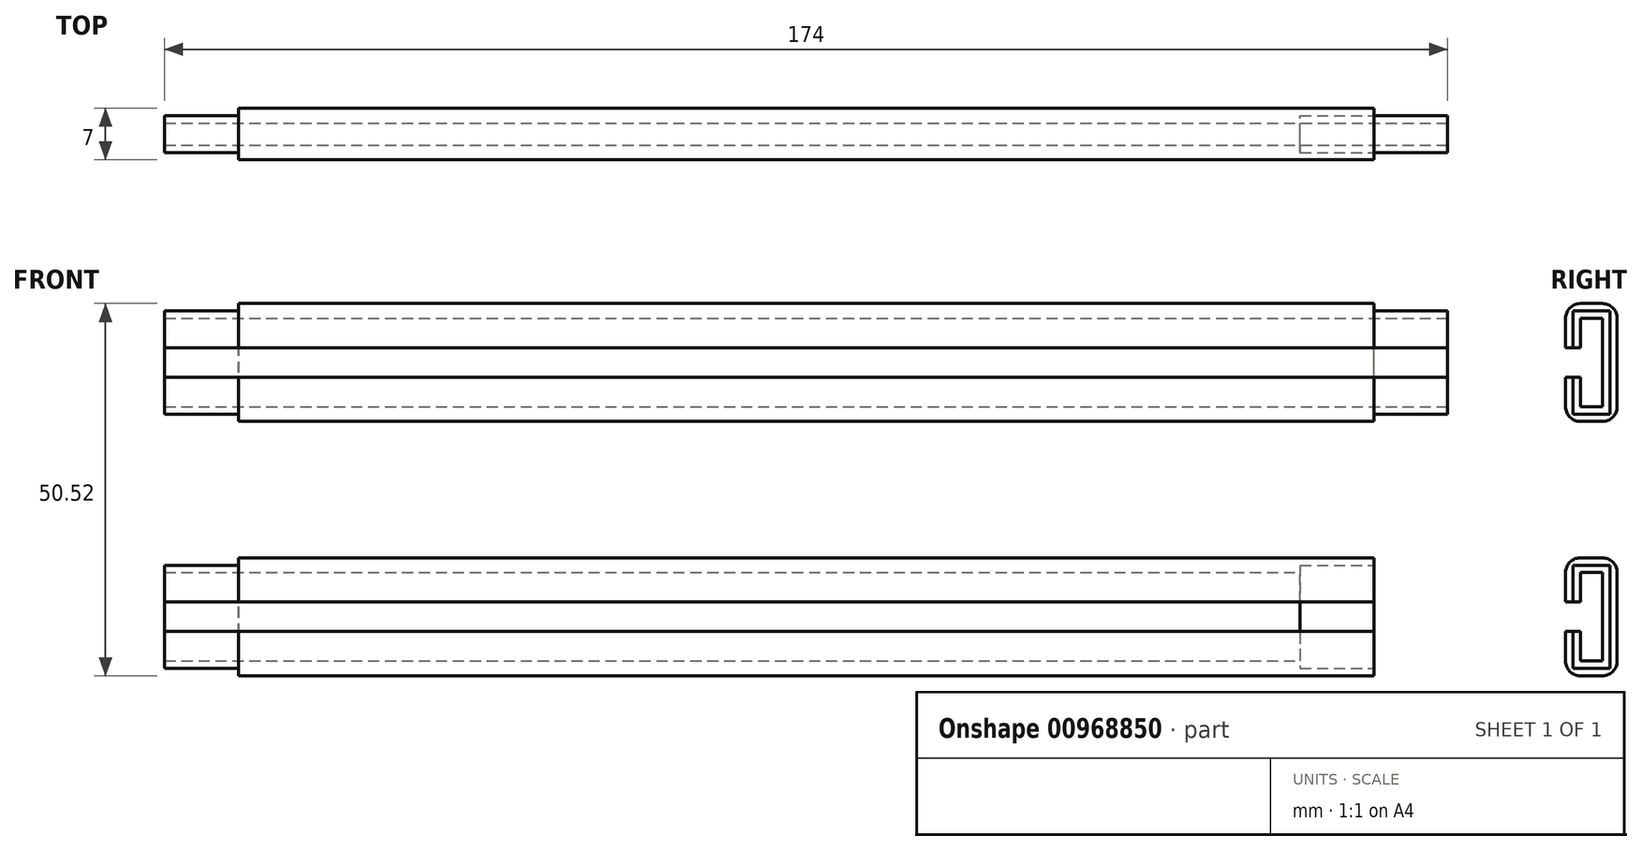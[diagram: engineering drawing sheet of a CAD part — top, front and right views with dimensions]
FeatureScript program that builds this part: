
annotation { "Feature Type Name" : "Feature", "Feature Type Description" : "" }
export const myFeature = defineFeature(function(context is Context, id is Id, definition is map)
    precondition{}
    {
        {
            var Q0;
            Q0=qCreatedBy(makeId("Front.planeOp"),FACE);
            var sketch = newSketch(context, id + "F0", { "sketchPlane" : qUnion([Q0])});
            skLineSegment(sketch, "E0.bottom", {"start": v(-19.62, 9.26) * mm, "end": v(144.38, 9.26) * mm});
            skLineSegment(sketch, "E0.top", {"start": v(-19.62, 25.26) * mm, "end": v(144.38, 25.26) * mm});
            skLineSegment(sketch, "E0.left", {"start": v(-19.62, 9.26) * mm, "end": v(-19.62, 25.26) * mm});
            skLineSegment(sketch, "E0.right", {"start": v(144.38, 9.26) * mm, "end": v(144.38, 25.26) * mm});
            skSolve(sketch);
        }
        {
            var Q0;
            Q0=makeQuery(id+"F0.imprint","IMPRINT",FACE,{"disambiguationData":[TD([[makeQuery(id+"F0.imprint","IMPRINT",EDGE,{"derivedFrom":sQuery(id+"F0.wireOp",EDGE,"E0.bottom")}),1.0]])]});
            extrude(context, id + "F1", {"entities" : qUnion([Q0]), "depth" : 7 * mm, "offsetDistance" : 25 * mm});
        }
        {
            var Q0;
            Q0=makeQuery(id+"F1.opExtrude","SWEPT_FACE",FACE,{"disambiguationData":[OSD([sQuery(id+"F0.wireOp",EDGE,"E0.right")])]});
            var sketch = newSketch(context, id + "F2", { "sketchPlane" : qUnion([Q0])});
            skLineSegment(sketch, "E1", {"start": v(-7, 15.26) * mm, "end": v(-5, 15.26) * mm});
            skLineSegment(sketch, "E2", {"start": v(-5, 15.26) * mm, "end": v(-5, 11.26) * mm});
            skLineSegment(sketch, "E3", {"start": v(-5, 11.26) * mm, "end": v(-2, 11.26) * mm});
            skLineSegment(sketch, "E4", {"start": v(-2, 11.26) * mm, "end": v(-2, 23.26) * mm});
            skLineSegment(sketch, "E5", {"start": v(-2, 23.26) * mm, "end": v(-5, 23.26) * mm});
            skLineSegment(sketch, "E6", {"start": v(-5, 23.26) * mm, "end": v(-5, 19.26) * mm});
            skLineSegment(sketch, "E7", {"start": v(-5, 19.26) * mm, "end": v(-7, 19.26) * mm});
            skLineSegment(sketch, "E8", {"start": v(-7, 19.26) * mm, "end": v(-7, 15.26) * mm});
            skSolve(sketch);
        }
        {
            var Q0;
            Q0=makeQuery(id+"F2.imprint","IMPRINT",FACE,{"disambiguationData":[TD([[makeQuery(id+"F2.imprint","IMPRINT",EDGE,{"derivedFrom":sQuery(id+"F2.wireOp",EDGE,"E1")}),1.0]])]});
            extrude(context, id + "F3", {"entities" : qUnion([Q0]), "operationType" : NewBodyOperationType.REMOVE, "endBound" : BoundingType.THROUGH_ALL, "oppositeDirection" : true, "depth" : 25 * mm, "offsetDistance" : 25 * mm});
        }
        {
            var Q0;
            Q0=makeQuery(id+"F1.opExtrude","SWEPT_FACE",FACE,{"disambiguationData":[OSD([sQuery(id+"F0.wireOp",EDGE,"E0.right")])]});
            var sketch = newSketch(context, id + "F4", { "sketchPlane" : qUnion([Q0])});
            skLineSegment(sketch, "E9.bottom", {"start": v(-6, 10.26) * mm, "end": v(-1, 10.26) * mm});
            skLineSegment(sketch, "E9.top", {"start": v(-6, 24.26) * mm, "end": v(-1, 24.26) * mm});
            skLineSegment(sketch, "E9.left", {"start": v(-6, 10.26) * mm, "end": v(-6, 24.26) * mm});
            skLineSegment(sketch, "E9.right", {"start": v(-1, 10.26) * mm, "end": v(-1, 24.26) * mm});
            skSolve(sketch);
        }
        {
            var Q0;
            {var subQ1=sQuery(id+"F4.wireOp",EDGE,"E9.bottom");Q0=makeQuery(id+"F4.imprint","IMPRINT",FACE,{"disambiguationData":[TD([[makeQuery(id+"F4.imprint","IMPRINT",EDGE,{"derivedFrom":subQ1}),1.0]])]});}
            extrude(context, id + "F5", {"entities" : qUnion([Q0]), "operationType" : NewBodyOperationType.ADD, "depth" : 10 * mm, "offsetDistance" : 25 * mm});
        }
        {
            var Q0;
            Q0=makeQuery(id+"F1.opExtrude","SWEPT_FACE",FACE,{"disambiguationData":[OSD([sQuery(id+"F0.wireOp",EDGE,"E0.left")])]});
            var sketch = newSketch(context, id + "F6", { "sketchPlane" : qUnion([Q0])});
            skLineSegment(sketch, "E10.bottom", {"start": v(6, 24.26) * mm, "end": v(1, 24.26) * mm});
            skLineSegment(sketch, "E10.top", {"start": v(6, 10.26) * mm, "end": v(1, 10.26) * mm});
            skLineSegment(sketch, "E10.left", {"start": v(6, 24.26) * mm, "end": v(6, 10.26) * mm});
            skLineSegment(sketch, "E10.right", {"start": v(1, 24.26) * mm, "end": v(1, 10.26) * mm});
            skSolve(sketch);
        }
        {
            var Q0;
            {var subQ8=sQuery(id+"F6.wireOp",EDGE,"E10.bottom");Q0=makeQuery(id+"F6.imprint","IMPRINT",FACE,{"disambiguationData":[TD([[makeQuery(id+"F6.imprint","IMPRINT",EDGE,{"derivedFrom":subQ8}),-1.0]])]});}
            extrude(context, id + "F7", {"entities" : qUnion([Q0]), "operationType" : NewBodyOperationType.REMOVE, "oppositeDirection" : true, "depth" : 10 * mm, "offsetDistance" : 25 * mm});
        }
        {
            var Q0;
            Q0=makeQuery(id+"F1.opExtrude","CAP_EDGE",EDGE,{"disambiguationData":[OSD([sQuery(id+"F0.wireOp",EDGE,"E0.top")])],"isStart":false});
            var Q1;
            Q1=makeQuery(id+"F1.opExtrude","CAP_EDGE",EDGE,{"disambiguationData":[OSD([sQuery(id+"F0.wireOp",EDGE,"E0.bottom")])],"isStart":false});
            var Q2;
            Q2=makeQuery(id+"F1.opExtrude","CAP_EDGE",EDGE,{"disambiguationData":[OSD([sQuery(id+"F0.wireOp",EDGE,"E0.top")])],"isStart":true});
            var Q3;
            Q3=makeQuery(id+"F1.opExtrude","CAP_EDGE",EDGE,{"disambiguationData":[OSD([sQuery(id+"F0.wireOp",EDGE,"E0.bottom")])],"isStart":true});
            fillet(context, id + "F8", {"entities" : qUnion([Q0, Q1, Q2, Q3]), "radius" : 2 * mm, "tangentPropagation" : true, "allowEdgeOverflow" : false});
        }
        {
            var Q0;
            Q0=makeQuery(id+"F1.opExtrude","SWEPT_BODY",BODY,{"disambiguationData":[OSD([sQuery(id+"F0.wireOp",EDGE,"E0.bottom"),sQuery(id+"F0.wireOp",EDGE,"E0.top"),sQuery(id+"F0.wireOp",EDGE,"E0.left"),sQuery(id+"F0.wireOp",EDGE,"E0.right")])]});
            var Q1;
            Q1=qCreatedBy(makeId("Top.planeOp"),FACE);
            mirror(context, id + "F9", {"entities" : qUnion([Q0]), "mirrorPlane" : qUnion([Q1])});
        }
        {
            var Q0;
            Q0=makeQuery(id+"F9.opPattern","COPY",FACE,{"derivedFrom":makeQuery(id+"F5.opExtrude","CAP_FACE",FACE,{"disambiguationData":[OSD([sQuery(id+"F2.wireOp",EDGE,"E1"),sQuery(id+"F2.wireOp",EDGE,"E2"),sQuery(id+"F2.wireOp",EDGE,"E3"),sQuery(id+"F2.wireOp",EDGE,"E4"),sQuery(id+"F2.wireOp",EDGE,"E5"),sQuery(id+"F2.wireOp",EDGE,"E6"),sQuery(id+"F2.wireOp",EDGE,"E7"),sQuery(id+"F4.wireOp",EDGE,"E9.bottom"),sQuery(id+"F4.wireOp",EDGE,"E9.top"),sQuery(id+"F4.wireOp",EDGE,"E9.left"),sQuery(id+"F4.wireOp",EDGE,"E9.right")])],"isStart":false}),"instanceName":"1"});
            extrude(context, id + "F10", {"entities" : qUnion([Q0]), "operationType" : NewBodyOperationType.REMOVE, "oppositeDirection" : true, "depth" : 20 * mm, "offsetDistance" : 25 * mm});
        }
    });
